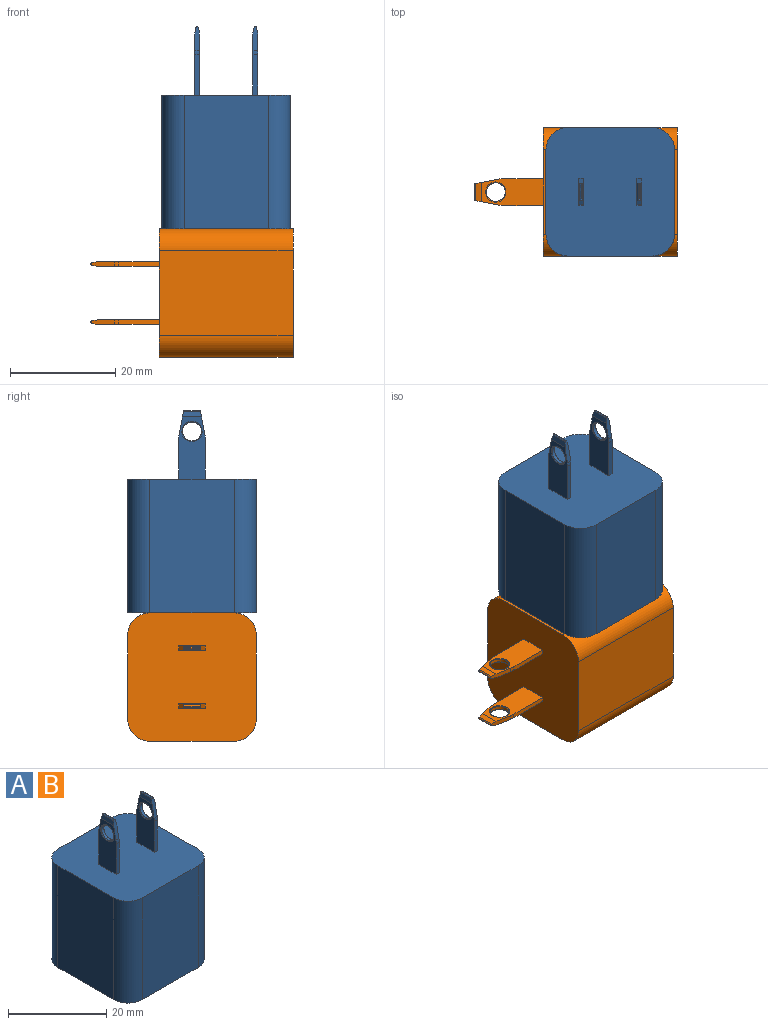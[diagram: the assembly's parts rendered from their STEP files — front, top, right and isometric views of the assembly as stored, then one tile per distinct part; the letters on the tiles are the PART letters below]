
ASSEMBLY  parts=2 mates=1
PART A: 42 faces, bbox 24.4x24.4x38.4 mm
  f0: plane 3.17x0.04mm, normal (0,0,1), area 0.1mm2, adj f27,f30,f34,f35
  f1: plane 11.81x5.08mm, normal (1,0,0), area 45.7mm2, adj f3,f26,f27,f28,f29,f30,f31,f33
  f2: plane 11.81x5.08mm, normal (-1,0,0), area 45.7mm2, adj f3,f26,f27,f28,f29,f30,f31,f32
  f3: plane 24.4x24.4mm, normal (0,0,1), area 571.3mm2, adj f1,f2,f5,f6,f7,f8,f9,f10
  f4: plane 3.17x0.04mm, normal (0,0,1), area 0.1mm2, adj f18,f21,f24,f25
  f5: plane 11.81x5.08mm, normal (1,0,0), area 45.7mm2, adj f3,f15,f17,f18,f19,f20,f21,f22
  f6: plane 25.4x16.01mm, normal (1,0,0), area 406.7mm2, adj f3,f7,f13,f14
  f7: cylinder r=4.19mm len=25.4mm, axis (0,0,-1), area 167.3mm2, adj f3,f6,f8,f14
  f8: plane 25.4x16.01mm, normal (0,1,0), area 406.7mm2, adj f3,f7,f9,f14
  f9: cylinder r=4.19mm len=25.4mm, axis (0,0,-1), area 167.3mm2, adj f3,f8,f10,f14
  f10: plane 25.4x16.01mm, normal (-1,0,0), area 406.7mm2, adj f3,f9,f11,f14
  f11: cylinder r=4.19mm len=25.4mm, axis (0,0,-1), area 167.3mm2, adj f3,f10,f12,f14
  f12: plane 25.4x16.01mm, normal (0,-1,0), area 406.7mm2, adj f3,f11,f13,f14
  f13: cylinder r=4.19mm len=25.4mm, axis (0,0,-1), area 167.3mm2, adj f3,f6,f12,f14
  f14: plane 24.4x24.4mm, normal (0,0,-1), area 580.3mm2, adj f6,f7,f8,f9,f10,f11,f12,f13
  f15: plane 7.7x0.88mm, normal (0,1,0), area 6.8mm2, adj f3,f5,f16,f17
  f16: plane 11.81x5.08mm, normal (-1,0,0), area 45.7mm2, adj f3,f15,f17,f18,f19,f20,f21,f23
  f17: cylinder r=4.19mm len=0.88mm, axis (-1,0,0), area 0.7mm2, adj f5,f15,f16,f18
  f18: plane 4.51x0.9mm, normal (0,0.98,0.19), area 3.7mm2, adj f4,f5,f16,f17,f22,f23,f24,f25
  f19: plane 7.7x0.88mm, normal (0,-1,0), area 6.8mm2, adj f3,f5,f16,f20
  f20: cylinder r=4.19mm len=0.88mm, axis (-1,0,0), area 0.7mm2, adj f5,f16,f19,f21
  f21: plane 4.51x0.9mm, normal (0,-0.98,0.19), area 3.7mm2, adj f4,f5,f16,f20,f22,f23,f24,f25
  f22: plane 3.64x1.03mm, normal (0.98,0,0.21), area 3.6mm2, adj f5,f18,f21,f24
  f23: plane 3.64x1.03mm, normal (-0.98,0,0.21), area 3.6mm2, adj f16,f18,f21,f25
  f24: bspline ~3.55x0.2mm, area 0.9mm2, adj f4,f18,f21,f22
  f25: bspline ~3.55x0.2mm, area 0.9mm2, adj f4,f18,f21,f23
  f26: plane 7.7x0.88mm, normal (0,1,0), area 6.8mm2, adj f1,f2,f3,f28
  f27: plane 4.51x0.9mm, normal (0,0.98,0.19), area 3.7mm2, adj f0,f1,f2,f28,f32,f33,f34,f35
  f28: cylinder r=4.19mm len=0.88mm, axis (1,0,0), area 0.7mm2, adj f1,f2,f26,f27
  f29: plane 7.7x0.88mm, normal (0,-1,0), area 6.8mm2, adj f1,f2,f3,f31
  f30: plane 4.51x0.9mm, normal (0,-0.98,0.19), area 3.7mm2, adj f0,f1,f2,f31,f32,f33,f34,f35
  f31: cylinder r=4.19mm len=0.88mm, axis (1,0,0), area 0.7mm2, adj f1,f2,f29,f30
  f32: plane 3.64x1.03mm, normal (-0.98,0,0.21), area 3.6mm2, adj f2,f27,f30,f34
  f33: plane 3.64x1.03mm, normal (0.98,0,0.21), area 3.6mm2, adj f1,f27,f30,f35
  f34: bspline ~3.55x0.2mm, area 0.9mm2, adj f0,f27,f30,f32
  f35: bspline ~3.55x0.2mm, area 0.9mm2, adj f0,f27,f30,f33
  f36: cylinder r=1.79mm len=3.58mm, axis (-1,0,0), area 7.1mm2, adj f40,f41
  f37: cylinder r=1.79mm len=3.58mm, axis (-1,0,0), area 7.1mm2, adj f38,f39
  f38: torus R=1.92mm, axis (1,0,0), area 2.3mm2, adj f1,f37
  f39: torus R=1.92mm, axis (1,0,0), area 2.3mm2, adj f2,f37
  f40: torus R=1.92mm, axis (1,0,0), area 2.3mm2, adj f5,f36
  f41: torus R=1.92mm, axis (1,0,0), area 2.3mm2, adj f16,f36
PART B: same geometry as A
PLACE A t=(-4.54,-20.25,26.18)mm
PLACE B rot(axis=(0,-1,0),90deg) t=(8.16,-20.25,13.98)mm
MATE fastened A.f14 <-> B.f6  axis (0,0,-1) through (-4.54,-20.25,26.18)mm
